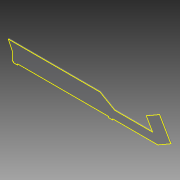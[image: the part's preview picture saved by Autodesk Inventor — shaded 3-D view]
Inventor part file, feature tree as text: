
AUTODESK INVENTOR PART (.ipt)
format: ipt  version: 2013 (Build 170138000, 138)  size: 154,624 bytes
history: native  units: in
note: dims shown in document units (in); Inventor stores cm internally (conversion verified against a paired STEP export)
features: reference x6, extrude x5, sketch x5
ambient origin geometry x8: Origin, YZ Plane, XZ Plane, XY Plane, X Axis, Y Axis, Z Axis, Center Point
bodies: Solid1 (feature_tree)
feature tree (16):
  extrude  "Extrusion1"  Depth=0.125in
  extrude  "Extrusion2"  Depth=1.0in
  extrude  "Extrusion6"  Depth=0.125in TaperAngle=0.0deg
  extrude  "Extrusion7"  Depth=1.0in
  extrude  "Extrusion8"  Depth=1.0in
  sketch  "Sketch9"  dims[d13=0.1718in d17=1.0in d19=150.0deg d21=1.0in d25=0.0in d36=8.5in d37=1.5in d44=3.0in d53=60.0deg d55=0.125in d56=0.0in d58=0.625in d59=0.125in d60=0.0in d61=1.5in d62=1.5in d63=0.125in d64=0.0in]
  sketch  "Sketch2"  dims[d0=0.125in d1=0.125in]
  reference  "Reference1"
  reference  "Reference2"
  reference  "Reference3"
  reference  "Reference4"
  reference  "Reference5"
  reference  "Reference6"
  sketch  "Sketch6"  dims[d2=0.5in d3=1.0in]
  sketch  "Sketch7"  dims[d4=12.125in d5=0.125in d6=0.0in]
  sketch  "Sketch8"  dims[d7=0.125in d8=0.0in d12=1.0in]
